# Revit family: Washfountain_Lavatory-Bradley_Corp-WF2608-Type_H_Drain
name_source: partatom
category: Plumbing Fixtures
revit_build: Autodesk Revit MEP 2012 (Build: 20110309_2315(x64)
units: mm (PartAtom-declared; Revit-internal decimal feet)

## types (2) — shared parameters
ADA Compliant = Yes
Assembly Code = D2010300
Buy American Act = No
Cold Lavatory Inlet = 1"
Cold Lavatory Inlet Radius = 1/2"
Description = Washfountain, 54" Circular with 9" Deep Bowl
Drain = 2"
Drain Radius = 1"
Flow Rate = 5.0 gal/min
Frequency = 50 Hz
Hot Lavatory Inlet = 1"
Hot Lavatory Inlet Radius = 1/2"
Industry Standards = ANSI Z124.3, Z124.6 and ANSI/ICPA SS-1-2001
Manufacturer = Bradley Corp
MasterFormat Number = 22 42 16
MasterFormat Title = Commercial Lavatories and Sinks
Material Note = Other Terrazzo colors available - See www.bradleycorp.com
Model = WF2608
OmniClass Table 21 Number = 21-04 20 10 60
OmniClass Table 21 Title = Plumbing Fixtures
OmniClass Table 23 Number = 23-31 13 00
OmniClass Table 23 Title = Sinks/Lavatories
Operating Water Pressure Range = 20 - 80 PSI
Pedestal Material = Metal - Bradley Corp - Stainless Steel - Satin
Product Tech Data URL - English = http://bradleycorp.com
Specifications URL = http://www.bradleycorp.com
URL = http://www.bradleycorp.com
Vent = 1 1/2"
Vent Radius = 3/4"
Version = 2.0
Voltage = 110 V
Width = 54 "
zero-valued in all types: CWFU, HWFU, WFU

## per-type parameters (varying)
| type | Juvenile Height | Model ID | Pedestal Height | Rim Height | Sensor Module Height | Spray Head Height | Standard Height |
| Standard | No | 2 | 19 " | 29.25 " | 39.125 " | 35.625 " | Yes |
| Juvenile | Yes | 1 | 15 " | 25.25 " | 35.125 " | 31.625 " | No |

## geometry (parser evidence)
native form markers: Blend x18
no freeform markers — native parametric forms only
